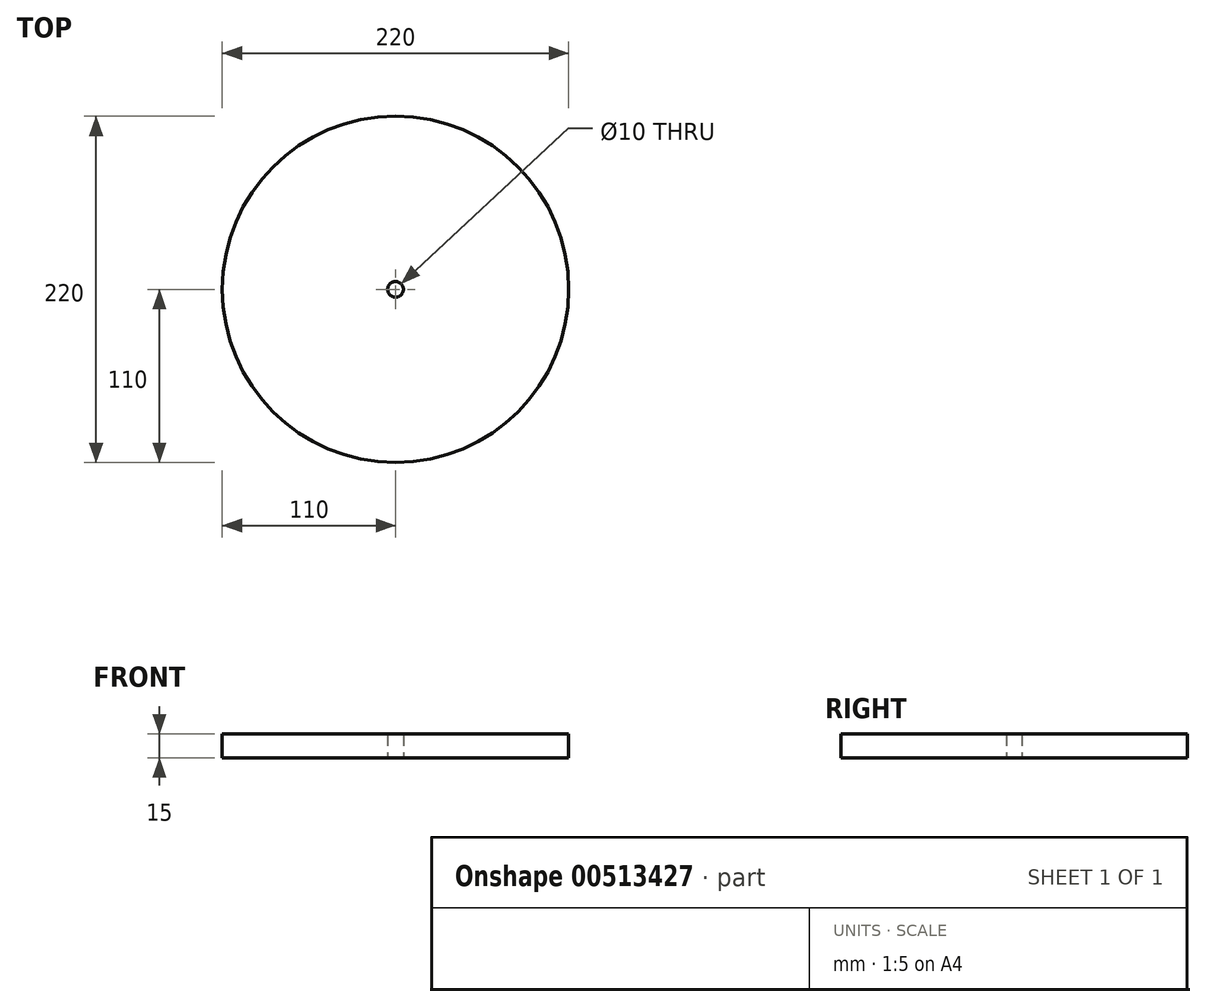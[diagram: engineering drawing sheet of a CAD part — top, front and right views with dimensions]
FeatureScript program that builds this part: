
annotation { "Feature Type Name" : "Feature", "Feature Type Description" : "" }
export const myFeature = defineFeature(function(context is Context, id is Id, definition is map)
    precondition{}
    {
        {
            var Q0;
            Q0=qCreatedBy(makeId("Top.planeOp"),FACE);
            var sketch = newSketch(context, id + "F0", { "sketchPlane" : qUnion([Q0])});
            skCircle(sketch, "E0", {"center": v(0, 0) * mm, "radius": 5 * mm});
            skCircle(sketch, "E1", {"center": v(0, 0) * mm, "radius": 110 * mm});
            skSolve(sketch);
        }
        {
            var Q0;
            Q0=makeQuery(id+"F0.imprint","IMPRINT",FACE,{"disambiguationData":[TD([[makeQuery(id+"F0.imprint","IMPRINT",EDGE,{"derivedFrom":sQuery(id+"F0.wireOp",EDGE,"E0")}),-1.0]])]});
            extrude(context, id + "F1", {"entities" : qUnion([Q0]), "depth" : 15 * mm});
        }
    });
